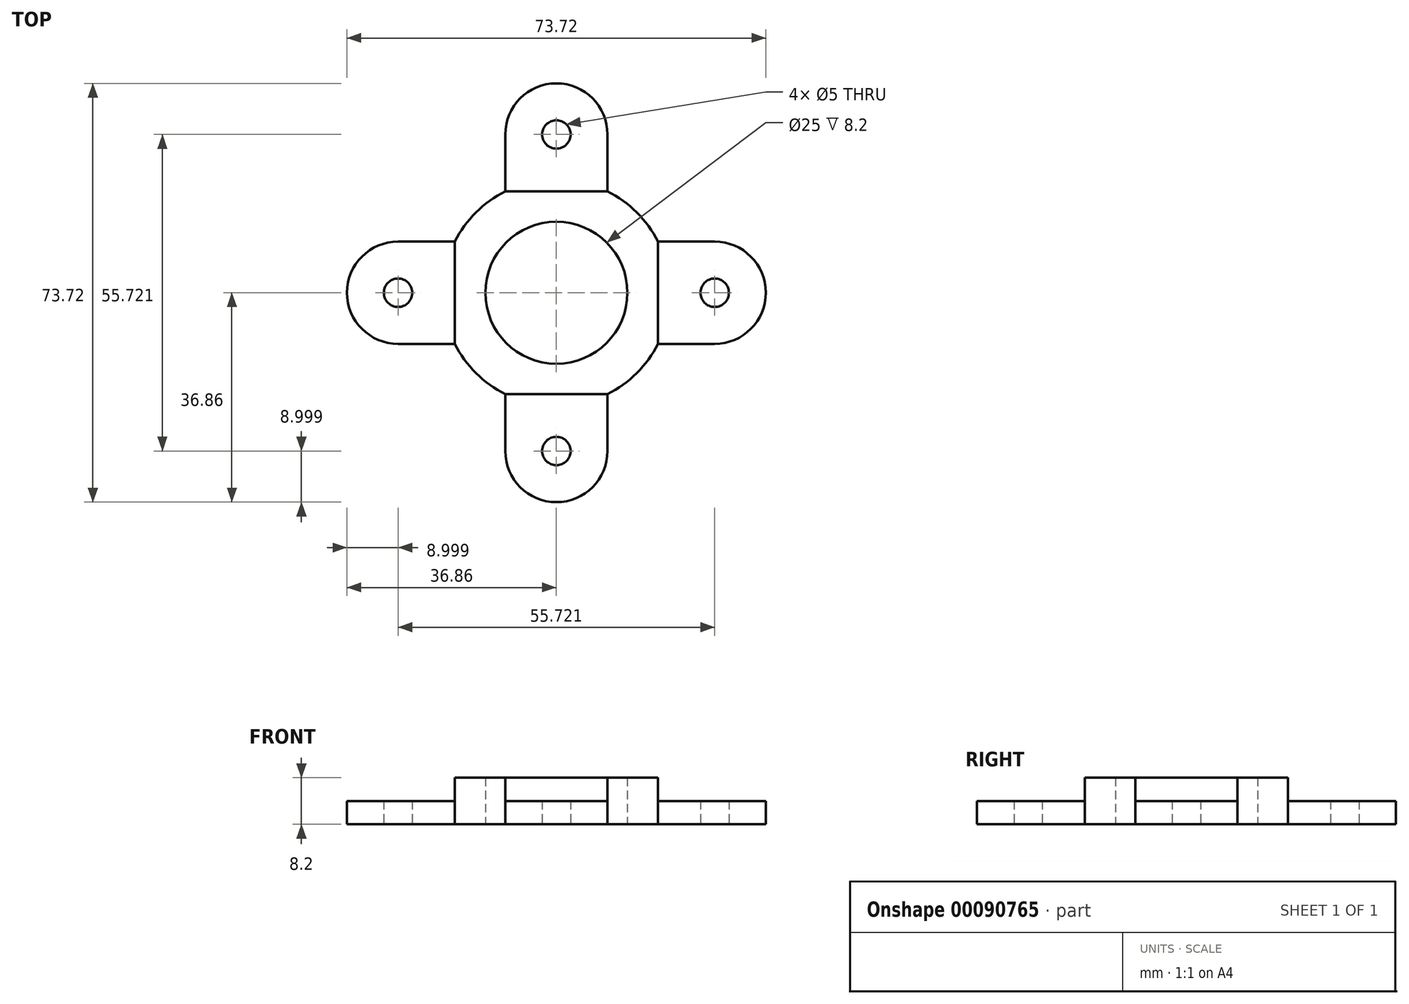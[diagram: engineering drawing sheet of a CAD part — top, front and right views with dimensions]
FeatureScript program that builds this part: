
annotation { "Feature Type Name" : "Feature", "Feature Type Description" : "" }
export const myFeature = defineFeature(function(context is Context, id is Id, definition is map)
    precondition{}
    {
        {
            var Q0;
            Q0=qCreatedBy(makeId("Top.planeOp"),FACE);
            var sketch = newSketch(context, id + "F0", { "sketchPlane" : qUnion([Q0])});
            skCircle(sketch, "E0", {"center": v(0, 0) * mm, "radius": 12.5 * mm});
            skArc(sketch, "E1", {"start": v(9, -17.86) * mm, "mid": v(14.14, -14.14) * mm, "end": v(17.86, -9) * mm});
            skLineSegment(sketch, "E2.left", {"start": v(9, -27.86) * mm, "end": v(9, -17.86) * mm});
            skLineSegment(sketch, "E2.right", {"start": v(-9, -27.86) * mm, "end": v(-9, -17.86) * mm});
            skLineSegment(sketch, "E3.MirrorCS", {"start": v(-9, 27.86) * mm, "end": v(-9, 17.86) * mm});
            skLineSegment(sketch, "E4.MirrorCS", {"start": v(9, 27.86) * mm, "end": v(9, 17.86) * mm});
            skArc(sketch, "E5.trimOffspring", {"start": v(-9, 17.86) * mm, "mid": v(-14.14, 14.14) * mm, "end": v(-17.86, 9) * mm});
            skLineSegment(sketch, "E6.bottom", {"start": v(-27.86, 9) * mm, "end": v(-17.86, 9) * mm});
            skLineSegment(sketch, "E6.top", {"start": v(-27.86, -9) * mm, "end": v(-17.86, -9) * mm});
            skLineSegment(sketch, "E7.MirrorCS", {"start": v(27.86, 9) * mm, "end": v(17.86, 9) * mm});
            skLineSegment(sketch, "E8.MirrorCS", {"start": v(27.86, -9) * mm, "end": v(17.86, -9) * mm});
            skArc(sketch, "E9.trimOffspring", {"start": v(-17.86, -9) * mm, "mid": v(-14.14, -14.14) * mm, "end": v(-9, -17.86) * mm});
            skArc(sketch, "E10.trimOffspring", {"start": v(17.86, 9) * mm, "mid": v(14.14, 14.14) * mm, "end": v(9, 17.86) * mm});
            skArc(sketch, "E11", {"start": v(9, 27.86) * mm, "mid": v(0, 36.86) * mm, "end": v(-9, 27.86) * mm});
            skArc(sketch, "E12", {"start": v(27.86, -9) * mm, "mid": v(36.86, 0) * mm, "end": v(27.86, 9) * mm});
            skArc(sketch, "E13.MirrorCS", {"start": v(-9, 27.86) * mm, "mid": v(0, 36.86) * mm, "end": v(9, 27.86) * mm});
            skArc(sketch, "E14.MirrorCS", {"start": v(9, -27.86) * mm, "mid": v(0, -36.86) * mm, "end": v(-9, -27.86) * mm});
            skArc(sketch, "E15.MirrorCS", {"start": v(-27.86, -9) * mm, "mid": v(-36.86, 0) * mm, "end": v(-27.86, 9) * mm});
            skPoint(sketch, "E16.MirrorCS.end.orphan", {"position": v(-9, 27.86) * mm});
            skPoint(sketch, "E17.orphan", {"position": v(27.86, 9) * mm});
            skLineSegment(sketch, "E18", {"start": v(-17.86, 9) * mm, "end": v(-17.86, -9) * mm});
            skLineSegment(sketch, "E19", {"start": v(17.86, 9) * mm, "end": v(17.86, -9) * mm});
            skLineSegment(sketch, "E20", {"start": v(9, -17.86) * mm, "end": v(-9, -17.86) * mm});
            skLineSegment(sketch, "E21", {"start": v(-9, 17.86) * mm, "end": v(9, 17.86) * mm});
            skCircle(sketch, "E22", {"center": v(-27.86, 0) * mm, "radius": 2.5 * mm});
            skCircle(sketch, "E23", {"center": v(0, -27.86) * mm, "radius": 2.5 * mm});
            skCircle(sketch, "E24", {"center": v(27.86, 0) * mm, "radius": 2.5 * mm});
            skCircle(sketch, "E25", {"center": v(0, 27.86) * mm, "radius": 2.5 * mm});
            skSolve(sketch);
        }
        {
            var Q0;
            Q0=makeQuery(id+"F0.imprint","IMPRINT",FACE,{"disambiguationData":[TD([[makeQuery(id+"F0.imprint","IMPRINT",EDGE,{"derivedFrom":sQuery(id+"F0.wireOp",EDGE,"E0")}),-1.0]])]});
            extrude(context, id + "F1", {"entities" : qUnion([Q0]), "depth" : 8.2 * mm});
        }
        {
            var Q0;
            Q0 = qSketchRegion(id + "F0", true);
            extrude(context, id + "F2", {"entities" : qUnion([Q0]), "operationType" : NewBodyOperationType.ADD, "depth" : 4.1 * mm});
        }
    });
